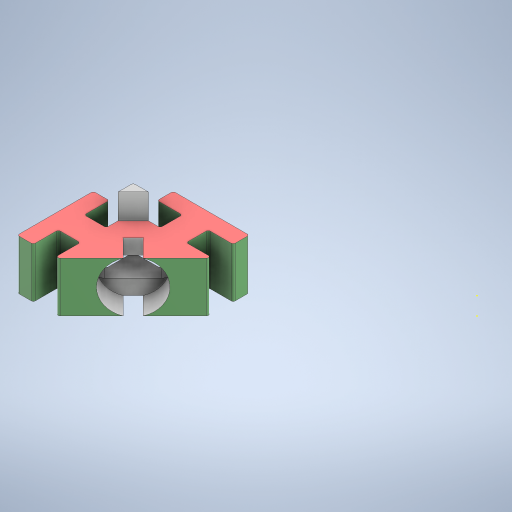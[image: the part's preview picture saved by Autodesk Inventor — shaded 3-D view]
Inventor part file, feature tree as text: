
AUTODESK INVENTOR PART (.ipt)
format: ipt  version: 2023 (Build 270158000, 158)  size: 356,864 bytes
history: native  units: in
note: dims shown in document units (in); Inventor stores cm internally (conversion verified against a paired STEP export)
features: sketch x6, other x4, extrude x3
ambient origin geometry x8: Origin, YZ Plane, XZ Plane, XY Plane, X Axis, Y Axis, Z Axis, Center Point
bodies: Body1 (feature_tree)
feature tree (13):
  other  "TmpPart3.ipt"
  sketch  "Sketch1"  dims[d0=0.3937in d1=0.2047in]
  extrude  "Extrusion1"  Depth=0.3937in
  sketch  "Sketch3"  dims[d5=0.0787in d6=0.126in d7=0.0in]
  sketch  "Sketch4"  dims[d8=0.0394in]
  extrude  "Extrusion2"  Depth=0.0787in
  extrude  "Extrusion3"  Depth=0.0787in TaperAngle=0.0deg
  other  "PLA2::TmpPart3.ipt"
  other  "TaggingFeature1"
  sketch  "Sketch2"  dims[d2=0.0984in d3=0.0in d4=0.0787in]
  sketch  "Sketch5"  dims[d9=90.0deg]
  sketch  "Sketch6"  dims[d10=0.0394in d11=180.0deg d12=45.0deg d13=0.0984in d14=0.0in]
  other  "PLA2"
